SOLIDWORKS PART (.sldprt)
format: sldprt  version: not decoded by parser v0  size: 242,688 bytes
history: native  units: mm
features: sketch x7, plane x2, material x1, sweep x1, extrude x1, mirror x1 (+12 scaffold rows collapsed)
feature tree (25):
  scaffold x12  (default folders/planes/origin — collapsed)
  material  "Material <not specified>"
  sketch  "Sketch1"  dims[c1.D3=3.6576mm c1.D5=2.36mm c1.D6=2.3mm c1.D7=2.3622mm c2.D5=2.36mm c2.D1=16.002mm c2.D2=1.6mm c2.D3=4.7244mm c2.D6=3.1622mm c3.D5=3.1622mm c3.D4=0.3556mm]
  sketch  "Sketch2"  dims[c1.D2=16.002mm c1.D3=~18.076856mm c1.D1=1054.1mm c2.D3=3.03mm]
  sweep  "Sweep1"
  sketch  "Sketch3"
  plane  "Plane1"  Offset=12.7mm
  sketch  "Sketch4"  dims[D1=5.556mm]
  sketch  "Sketch6"
  sketch  "Sketch7"  dims[D1=0.3556mm]
  sketch  "Sketch8"
  extrude  "Extrude1"  Depth=34.925mm
  mirror  "Mirror1"
  plane  "Plane2"
decode coverage: 5 of 10 modeling features carry decoded parameters
note: ~ marks probable driven/reference dimensions
note: suppression state not decoded; provenance and decode notes live in map.json
